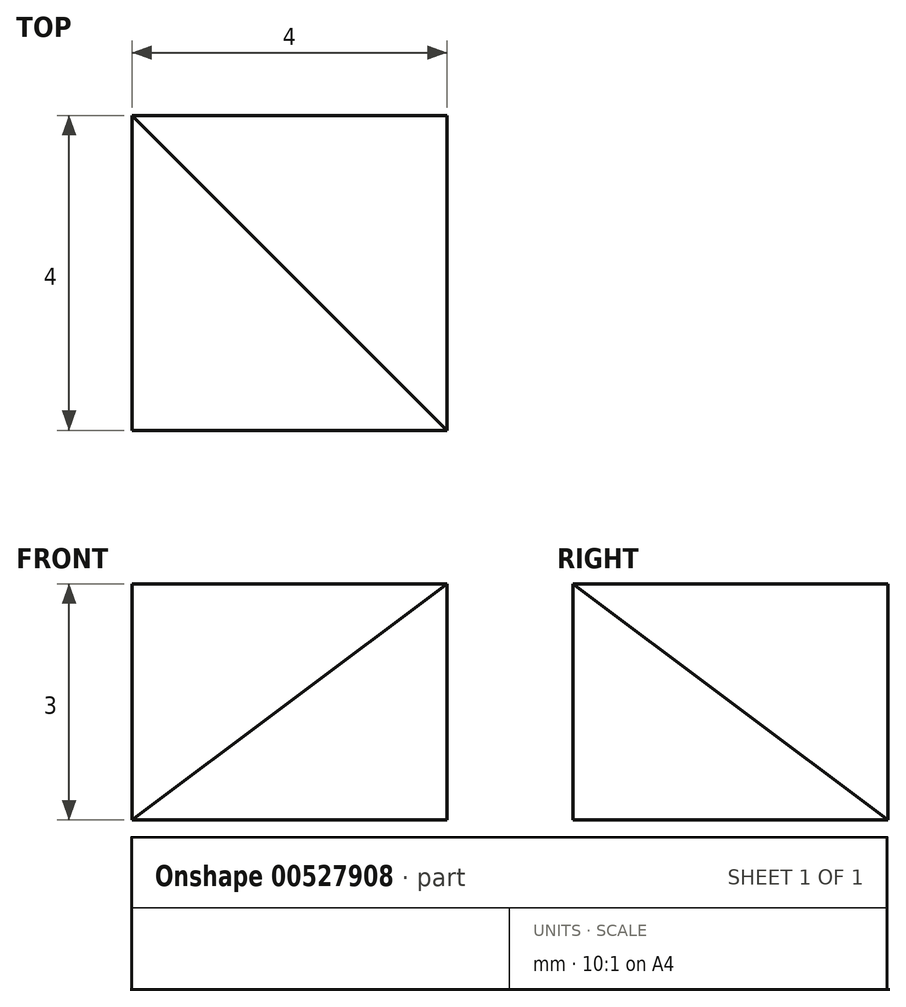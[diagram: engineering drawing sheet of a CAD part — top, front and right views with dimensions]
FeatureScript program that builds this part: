
annotation { "Feature Type Name" : "Feature", "Feature Type Description" : "" }
export const myFeature = defineFeature(function(context is Context, id is Id, definition is map)
    precondition{}
    {
        {
            var Q0;
            Q0=qCreatedBy(makeId("Top.planeOp"),FACE);
            var sketch = newSketch(context, id + "F0", { "sketchPlane" : qUnion([Q0])});
            skLineSegment(sketch, "E0.bottom", {"start": v(0, 0) * mm, "end": v(4, 0) * mm});
            skLineSegment(sketch, "E0.top", {"start": v(0, 4) * mm, "end": v(4, 4) * mm});
            skLineSegment(sketch, "E0.left", {"start": v(0, 0) * mm, "end": v(0, 4) * mm});
            skLineSegment(sketch, "E0.right", {"start": v(4, 0) * mm, "end": v(4, 4) * mm});
            skSolve(sketch);
        }
        {
            var Q0;
            Q0=qSketchRegion(id+"F0",true);
            extrude(context, id + "F1", {"entities" : qUnion([Q0]), "depth" : 3 * mm});
        }
        {
            var Q0;
            Q0=qCreatedBy(makeId("Origin.pointOp"),VERTEX);
            var Q1;
            Q1=makeQuery(id+"F1.opExtrude","CAP_VERTEX",VERTEX,{"disambiguationData":[OSD([sQuery(id+"F0.wireOp",EDGE,"E0.bottom"),sQuery(id+"F0.wireOp",EDGE,"E0.right")])],"isStart":false});
            var Q2;
            Q2=makeQuery(id+"F1.opExtrude","CAP_VERTEX",VERTEX,{"disambiguationData":[OSD([sQuery(id+"F0.wireOp",EDGE,"E0.top"),sQuery(id+"F0.wireOp",EDGE,"E0.left")])],"isStart":false});
            cPlane(context, id + "F2", {"entities" : qUnion([Q0, Q1, Q2]), "cplaneType" : CPlaneType.THREE_POINT, "offset" : 25 * mm, "width" : 150 * mm, "height" : 150 * mm});
        }
        {
            var Q0;
            Q0=qCreatedBy(id+"F2.planeOp",FACE);
            var sketch = newSketch(context, id + "F3", { "sketchPlane" : qUnion([Q0])});
            skLineSegment(sketch, "E1.bottom", {"start": v(-4.2, -6.72) * mm, "end": v(13.39, -6.72) * mm});
            skLineSegment(sketch, "E1.top", {"start": v(-4.2, 4.72) * mm, "end": v(13.39, 4.72) * mm});
            skLineSegment(sketch, "E1.left", {"start": v(-4.2, -6.72) * mm, "end": v(-4.2, 4.72) * mm});
            skLineSegment(sketch, "E1.right", {"start": v(13.39, -6.72) * mm, "end": v(13.39, 4.72) * mm});
            skSolve(sketch);
        }
        {
            var Q0;
            Q0=qSketchRegion(id+"F3",true);
            extrude(context, id + "F4", {"entities" : qUnion([Q0]), "operationType" : NewBodyOperationType.REMOVE, "oppositeDirection" : true, "depth" : 25 * mm});
        }
        {
            var Q0;
            Q0=makeQuery(id+"F1.opExtrude","CAP_VERTEX",VERTEX,{"disambiguationData":[OSD([sQuery(id+"F0.wireOp",EDGE,"E0.top"),sQuery(id+"F0.wireOp",EDGE,"E0.left")])],"isStart":false});
            var Q1;
            Q1=makeQuery(id+"F1.opExtrude","CAP_VERTEX",VERTEX,{"disambiguationData":[OSD([sQuery(id+"F0.wireOp",EDGE,"E0.top"),sQuery(id+"F0.wireOp",EDGE,"E0.right")])],"isStart":true});
            var Q2;
            Q2=makeQuery(id+"F1.opExtrude","CAP_VERTEX",VERTEX,{"disambiguationData":[OSD([sQuery(id+"F0.wireOp",EDGE,"E0.bottom"),sQuery(id+"F0.wireOp",EDGE,"E0.right")])],"isStart":false});
            cPlane(context, id + "F5", {"entities" : qUnion([Q0, Q1, Q2]), "cplaneType" : CPlaneType.THREE_POINT, "offset" : 25 * mm, "width" : 150 * mm, "height" : 150 * mm});
        }
        {
            var Q0;
            Q0=qCreatedBy(id+"F5.planeOp",FACE);
            var sketch = newSketch(context, id + "F6", { "sketchPlane" : qUnion([Q0])});
            skLineSegment(sketch, "E2.bottom", {"start": v(-7.46, 5.21) * mm, "end": v(15.26, 5.21) * mm});
            skLineSegment(sketch, "E2.top", {"start": v(-7.46, -5.8) * mm, "end": v(15.26, -5.8) * mm});
            skLineSegment(sketch, "E2.left", {"start": v(-7.46, 5.21) * mm, "end": v(-7.46, -5.8) * mm});
            skLineSegment(sketch, "E2.right", {"start": v(15.26, 5.21) * mm, "end": v(15.26, -5.8) * mm});
            skSolve(sketch);
        }
        {
            var Q0;
            Q0=qSketchRegion(id+"F6",true);
            extrude(context, id + "F7", {"entities" : qUnion([Q0]), "operationType" : NewBodyOperationType.REMOVE, "depth" : 25 * mm});
        }
    });
